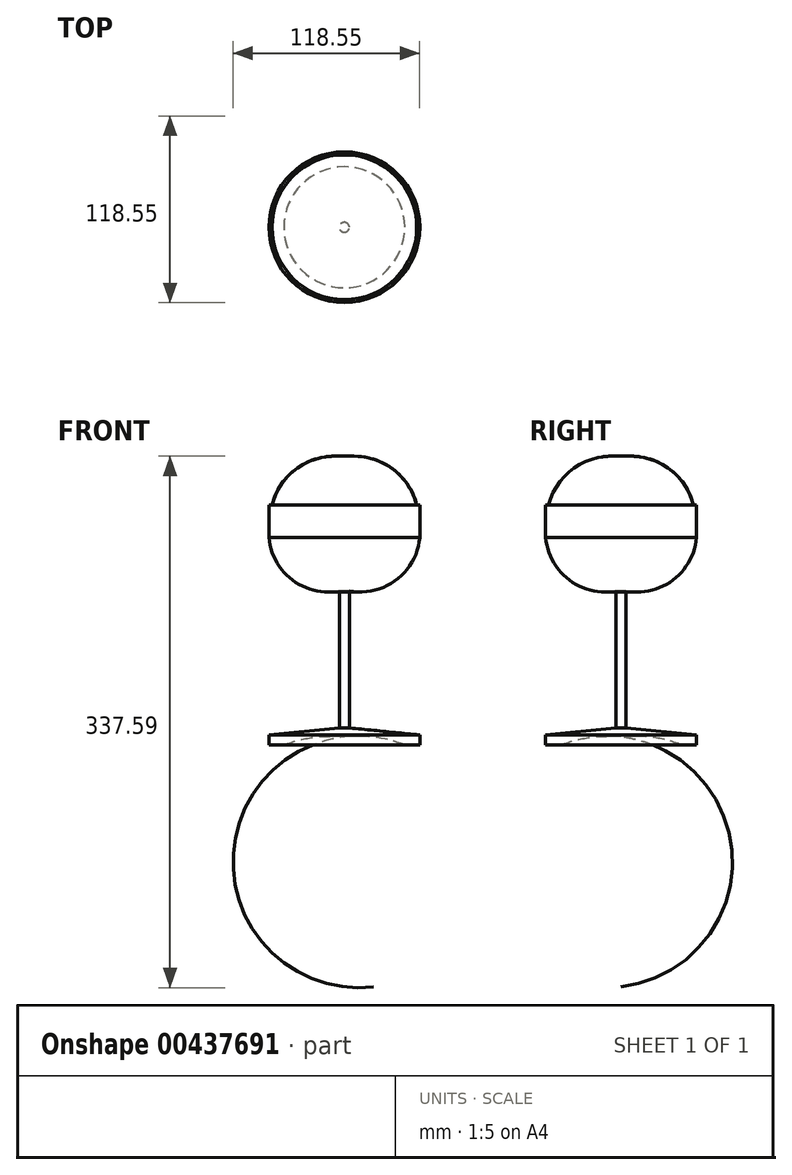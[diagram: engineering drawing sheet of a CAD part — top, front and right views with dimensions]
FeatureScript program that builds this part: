
annotation { "Feature Type Name" : "Feature", "Feature Type Description" : "" }
export const myFeature = defineFeature(function(context is Context, id is Id, definition is map)
    precondition{}
    {
        {
            var Q0;
            Q0=qCreatedBy(makeId("Front.planeOp"),FACE);
            var sketch = newSketch(context, id + "F0", { "sketchPlane" : qUnion([Q0])});
            skLineSegment(sketch, "E0", {"start": v(-38.4, 0.02) * mm, "end": v(-47.9, 0.02) * mm});
            skLineSegment(sketch, "E1", {"start": v(-47.9, 0.02) * mm, "end": v(-47.9, 6.37) * mm});
            skLineSegment(sketch, "E2", {"start": v(-47.9, 6.37) * mm, "end": v(-3.17, 10.85) * mm});
            skLineSegment(sketch, "E3", {"start": v(-3.18, 10.85) * mm, "end": v(-3.18, 97.78) * mm});
            skLineSegment(sketch, "E4", {"start": v(-47.9, 131.77) * mm, "end": v(-47.9, 152.42) * mm});
            skLineSegment(sketch, "E5", {"start": v(-47.9, 152.42) * mm, "end": v(-46, 152.42) * mm});
            skLineSegment(sketch, "E6", {"start": v(0, 101.9) * mm, "end": v(0, 5.02) * mm});
            skArc(sketch, "E7", {"start": v(-46, 152.42) * mm, "mid": v(-36.54, 114.83) * mm, "end": v(0, 101.9) * mm});
            skArc(sketch, "E8", {"start": v(-47.9, 131.77) * mm, "mid": v(-33.05, 104.89) * mm, "end": v(-3.17, 97.78) * mm});
            skArc(sketch, "E9", {"start": v(0, 5.02) * mm, "mid": v(-19.5, 4.88) * mm, "end": v(-38.4, 0.02) * mm});
            skLineSegment(sketch, "E10", {"start": v(0, 101.9) * mm, "end": v(0, 152.42) * mm});
            skLineSegment(sketch, "E11", {"start": v(0, 152.42) * mm, "end": v(-46, 152.42) * mm});
            skLineSegment(sketch, "E12.MirrorCS", {"start": v(47.9, 152.42) * mm, "end": v(46, 152.42) * mm});
            skLineSegment(sketch, "E13.MirrorCS", {"start": v(47.9, 0.02) * mm, "end": v(47.9, 6.37) * mm});
            skLineSegment(sketch, "E14.MirrorCS", {"start": v(0, 152.42) * mm, "end": v(46, 152.42) * mm});
            skArc(sketch, "E15.MirrorCS", {"start": v(0, 5.02) * mm, "mid": v(19.5, 4.88) * mm, "end": v(38.4, 0.02) * mm});
            skArc(sketch, "E16.MirrorCS", {"start": v(47.9, 131.77) * mm, "mid": v(33.05, 104.89) * mm, "end": v(3.17, 97.78) * mm});
            skArc(sketch, "E17.MirrorCS", {"start": v(46, 152.42) * mm, "mid": v(36.54, 114.83) * mm, "end": v(0, 101.9) * mm});
            skLineSegment(sketch, "E18.MirrorCS", {"start": v(47.9, 131.77) * mm, "end": v(47.9, 152.42) * mm});
            skLineSegment(sketch, "E19.MirrorCS", {"start": v(3.18, 10.85) * mm, "end": v(3.18, 97.78) * mm});
            skLineSegment(sketch, "E20.MirrorCS", {"start": v(38.4, 0.02) * mm, "end": v(47.9, 0.02) * mm});
            skLineSegment(sketch, "E21.MirrorCS", {"start": v(47.9, 6.37) * mm, "end": v(3.17, 10.85) * mm});
            skSolve(sketch);
        }
        {
            var Q0;
            Q0=makeQuery(id+"F0.imprint","IMPRINT",FACE,{"disambiguationData":[TD([[makeQuery(id+"F0.imprint","IMPRINT",EDGE,{"derivedFrom":sQuery(id+"F0.wireOp",EDGE,"E0")}),-1.0]])]});
            var Q1;
            Q1=sQuery(id+"F0.wireOp",EDGE,"E6");
            revolve(context, id + "F1", {"entities" : qUnion([Q0]), "axis" : qUnion([Q1]), "revolveType" : RevolveType.FULL});
        }
        {
            var Q0;
            Q0=makeQuery(id+"F0.imprint","IMPRINT",FACE,{"disambiguationData":[TD([[makeQuery(id+"F0.imprint","IMPRINT",EDGE,{"derivedFrom":sQuery(id+"F0.wireOp",EDGE,"E7")}),1.0]])]});
            var Q1;
            Q1=sQuery(id+"F0.wireOp",EDGE,"E10");
            revolve(context, id + "F2", {"entities" : qUnion([Q0]), "axis" : qUnion([Q1]), "revolveType" : RevolveType.FULL});
        }
    });
